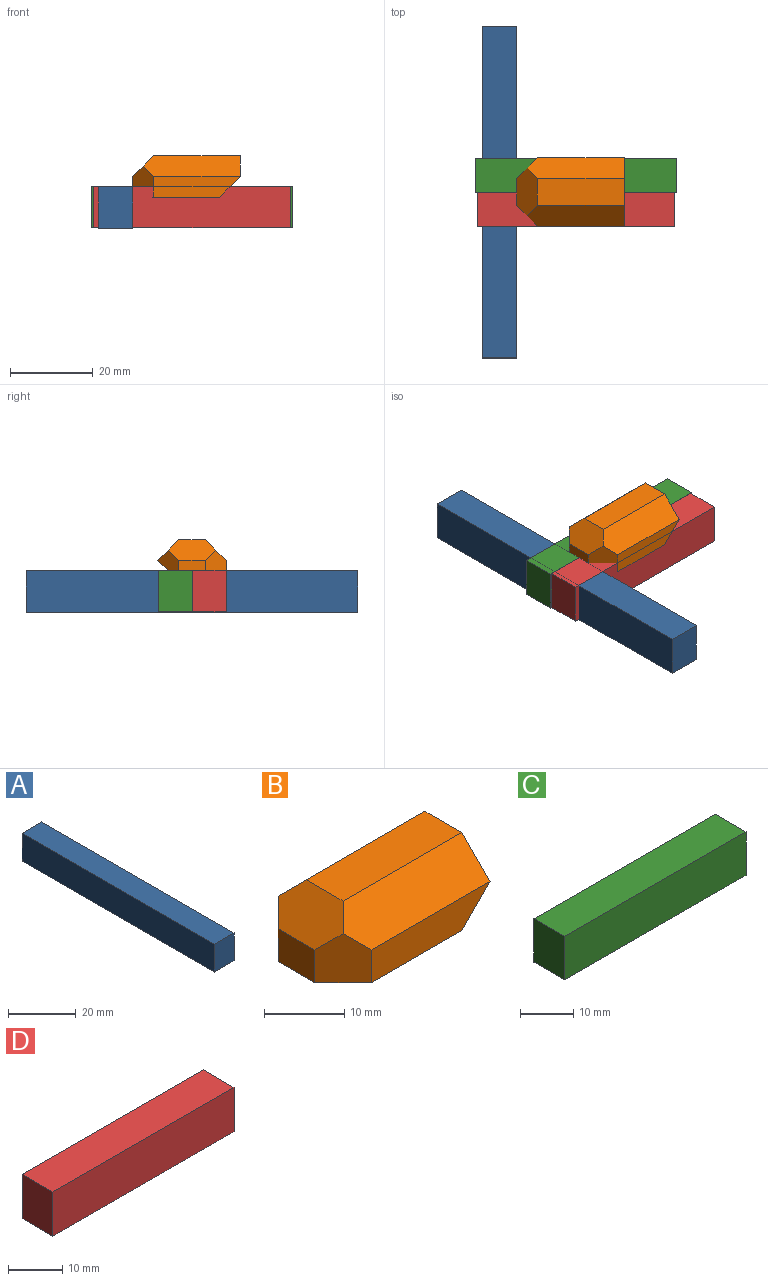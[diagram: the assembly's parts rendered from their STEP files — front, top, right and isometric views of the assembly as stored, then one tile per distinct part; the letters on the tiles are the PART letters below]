
ASSEMBLY  parts=4 mates=3
PART A: 6 faces, bbox 8.2x80x10 mm
  f0: plane 10x8.21mm, normal (0,1,0), area 82.1mm2, adj f1,f3,f4,f5
  f1: plane 80x10mm, normal (-1,0,0), area 800mm2, adj f0,f2,f4,f5
  f2: plane 10x8.21mm, normal (0,-1,0), area 82.1mm2, adj f1,f3,f4,f5
  f3: plane 80x10mm, normal (1,0,0), area 800mm2, adj f0,f2,f4,f5
  f4: plane 80x8.21mm, normal (0,0,1), area 656.5mm2, adj f0,f1,f2,f3
  f5: plane 80x8.21mm, normal (0,0,-1), area 656.5mm2, adj f0,f1,f2,f3
PART B: 12 faces, bbox 26x16.5x10 mm
  f0: plane 6.49x5mm, normal (-1,0,0), area 32.5mm2, adj f4,f6,f9,f11
  f1: plane 20.96x5mm, normal (0,-1,0), area 92.3mm2, adj f4,f7,f10,f11
  f2: plane 16.49x5mm, normal (1,0,0), area 57.5mm2, adj f3,f5,f7,f10
  f3: plane 20.96x6.49mm, normal (0,0,1), area 136mm2, adj f2,f5,f9,f10
  f4: plane 20.96x11.49mm, normal (0,0,-1), area 228.3mm2, adj f0,f1,f7,f8,f11
  f5: plane 23.46x5mm, normal (0,0.71,0.71), area 157mm2, adj f2,f3,f6,f8,f9
  f6: plane 7.5x5mm, normal (-0.71,0.71,0), area 26.5mm2, adj f0,f5,f8,f9
  f7: plane 16.49x5mm, normal (0.71,0,-0.71), area 98.9mm2, adj f1,f2,f4,f8
  f8: plane 25.96x5mm, normal (0,0.71,-0.71), area 148.2mm2, adj f4,f5,f6,f7
  f9: plane 11.49x5mm, normal (-0.71,0,0.71), area 63.6mm2, adj f0,f3,f5,f6,f10,f11
  f10: plane 23.46x5mm, normal (0,-0.71,0.71), area 157mm2, adj f1,f2,f3,f9,f11
  f11: plane 7.5x5mm, normal (-0.71,-0.71,0), area 44.2mm2, adj f0,f1,f4,f9,f10
PART C: 6 faces, bbox 48.2x8.2x10 mm
  f0: plane 48.21x10mm, normal (0,1,0), area 482.1mm2, adj f1,f3,f4,f5
  f1: plane 10x8.21mm, normal (-1,0,0), area 82.1mm2, adj f0,f2,f4,f5
  f2: plane 48.21x10mm, normal (0,-1,0), area 482.1mm2, adj f1,f3,f4,f5
  f3: plane 10x8.21mm, normal (1,0,0), area 82.1mm2, adj f0,f2,f4,f5
  f4: plane 48.21x8.21mm, normal (0,0,1), area 395.6mm2, adj f0,f1,f2,f3
  f5: plane 48.21x8.21mm, normal (0,0,-1), area 395.6mm2, adj f0,f1,f2,f3
PART D: 6 faces, bbox 47.4x8.1x10 mm
  f0: plane 47.4x10mm, normal (0,1,0), area 474mm2, adj f1,f3,f4,f5
  f1: plane 10x8.1mm, normal (-1,0,0), area 81mm2, adj f0,f2,f4,f5
  f2: plane 47.4x10mm, normal (0,-1,0), area 474mm2, adj f1,f3,f4,f5
  f3: plane 10x8.1mm, normal (1,0,0), area 81mm2, adj f0,f2,f4,f5
  f4: plane 47.4x8.1mm, normal (0,0,1), area 383.9mm2, adj f0,f1,f2,f3
  f5: plane 47.4x8.1mm, normal (0,0,-1), area 383.9mm2, adj f0,f1,f2,f3
PLACE A t=(51.41,-23.07,-2.5)mm
PLACE B t=(36.68,-40.54,5)mm
PLACE C t=(0.9,-63.21,-2.39)mm
PLACE D t=(1.31,0,-2.39)mm
MATE fastened C.f2 <-> D.f0  axis (0,-1,0) through (25.01,-29.53,2.61)mm
MATE fastened B.f1 <-> D.f2  axis (0,-1,0) through (25.01,-37.63,7.61)mm
MATE fastened A.f3 <-> B.f0  axis (1,0,0) through (10.72,-29.39,7.5)mm
